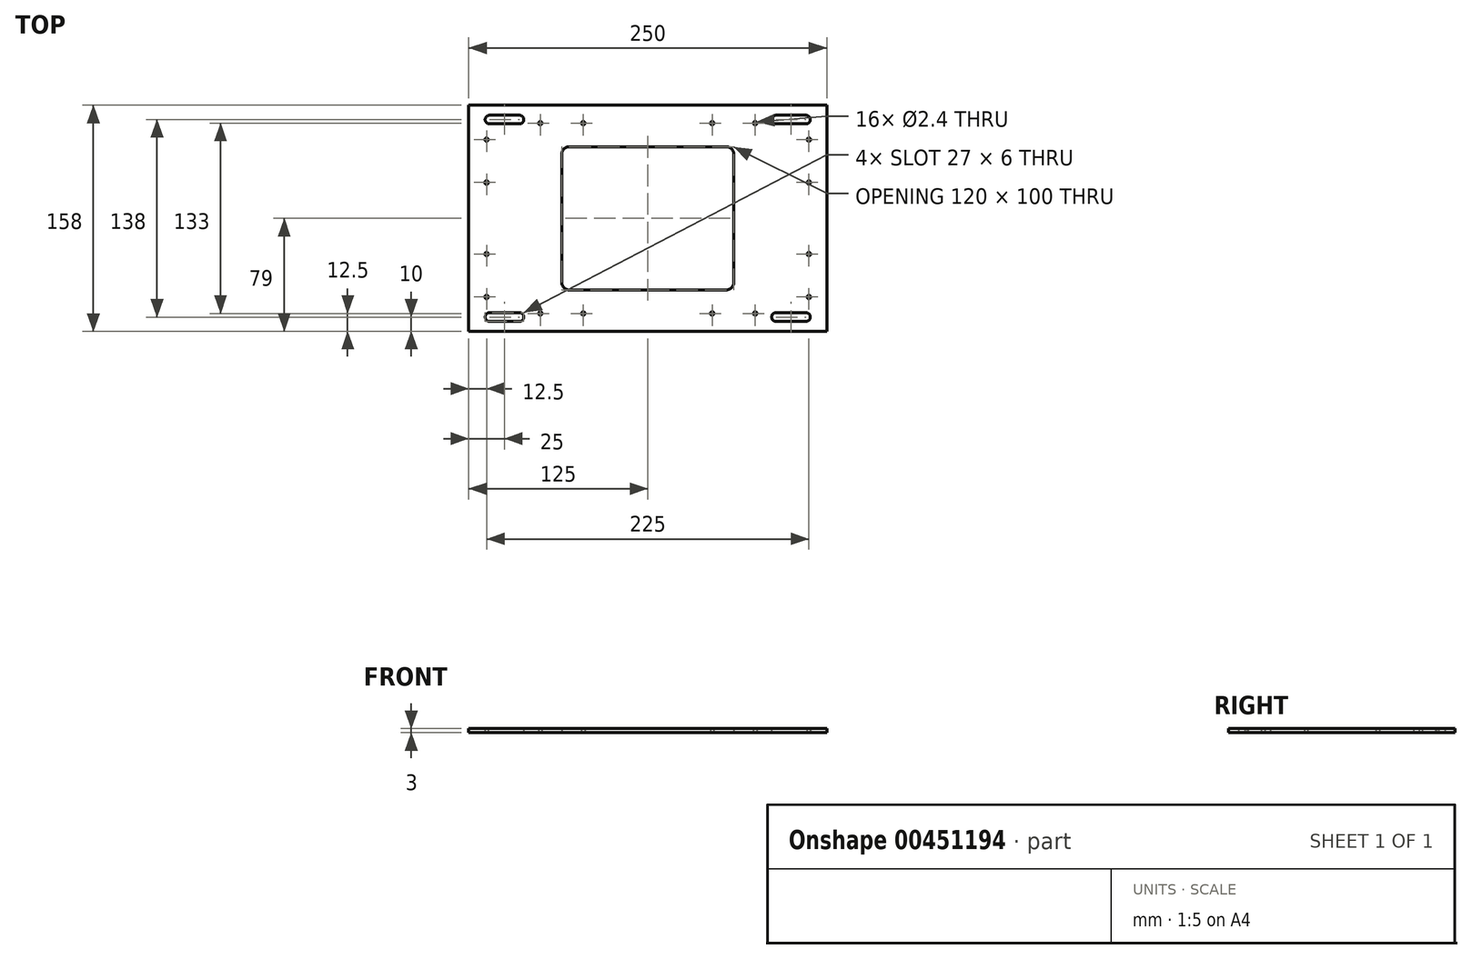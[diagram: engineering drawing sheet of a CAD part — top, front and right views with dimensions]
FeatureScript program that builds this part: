
annotation { "Feature Type Name" : "Feature", "Feature Type Description" : "" }
export const myFeature = defineFeature(function(context is Context, id is Id, definition is map)
    precondition{}
    {
        {
            var Q0;
            Q0=qCreatedBy(makeId("Top.planeOp"),FACE);
            var sketch = newSketch(context, id + "F0", { "sketchPlane" : qUnion([Q0])});
            skLineSegment(sketch, "E0.bottom", {"start": v(125, -79) * mm, "end": v(-125, -79) * mm});
            skLineSegment(sketch, "E0.top", {"start": v(125, 79) * mm, "end": v(-125, 79) * mm});
            skLineSegment(sketch, "E0.left", {"start": v(125, -79) * mm, "end": v(125, 79) * mm});
            skLineSegment(sketch, "E0.right", {"start": v(-125, -79) * mm, "end": v(-125, 79) * mm});
            skPoint(sketch, "E0.middle", {"position": v(0, 0) * mm});
            skCircle(sketch, "E1", {"center": v(-107.5, 69) * mm, "radius": 2.5 * mm, "construction": true});
            skCircle(sketch, "E2", {"center": v(-107.5, -69) * mm, "radius": 2.5 * mm, "construction": true});
            skLineSegment(sketch, "E3.bottom", {"start": v(60, -50) * mm, "end": v(-60, -50) * mm});
            skLineSegment(sketch, "E3.top", {"start": v(60, 50) * mm, "end": v(-60, 50) * mm});
            skLineSegment(sketch, "E3.left", {"start": v(60, -50) * mm, "end": v(60, 50) * mm});
            skLineSegment(sketch, "E3.right", {"start": v(-60, -50) * mm, "end": v(-60, 50) * mm});
            skCircle(sketch, "E4.MirrorC", {"center": v(107.5, -69) * mm, "radius": 2.5 * mm, "construction": true});
            skCircle(sketch, "E5.MirrorC", {"center": v(107.5, 69) * mm, "radius": 2.5 * mm, "construction": true});
            skCircle(sketch, "E6", {"center": v(-112.5, 55) * mm, "radius": 1.2 * mm});
            skCircle(sketch, "E7", {"center": v(-112.5, 25) * mm, "radius": 1.2 * mm});
            skCircle(sketch, "E8", {"center": v(-112.5, -25) * mm, "radius": 1.2 * mm});
            skCircle(sketch, "E9", {"center": v(-112.5, -55) * mm, "radius": 1.2 * mm});
            skCircle(sketch, "E10.MirrorC", {"center": v(112.5, -25) * mm, "radius": 1.2 * mm});
            skCircle(sketch, "E11.MirrorC", {"center": v(112.5, -55) * mm, "radius": 1.2 * mm});
            skCircle(sketch, "E12.MirrorC", {"center": v(112.5, 25) * mm, "radius": 1.2 * mm});
            skCircle(sketch, "E13.MirrorC", {"center": v(112.5, 55) * mm, "radius": 1.2 * mm});
            skCircle(sketch, "E14", {"center": v(-75, -66.5) * mm, "radius": 1.2 * mm});
            skCircle(sketch, "E15", {"center": v(-45, -66.5) * mm, "radius": 1.2 * mm});
            skCircle(sketch, "E16", {"center": v(45, -66.5) * mm, "radius": 1.2 * mm});
            skCircle(sketch, "E17", {"center": v(75, -66.5) * mm, "radius": 1.2 * mm});
            skCircle(sketch, "E18.MirrorC", {"center": v(45, 66.5) * mm, "radius": 1.2 * mm});
            skCircle(sketch, "E19.MirrorC", {"center": v(-75, 66.5) * mm, "radius": 1.2 * mm});
            skCircle(sketch, "E20.MirrorC", {"center": v(-45, 66.5) * mm, "radius": 1.2 * mm});
            skCircle(sketch, "E21.MirrorC", {"center": v(75, 66.5) * mm, "radius": 1.2 * mm});
            skLineSegment(sketch, "E22.bottom", {"start": v(-89.5, 66) * mm, "end": v(-110.5, 66) * mm});
            skLineSegment(sketch, "E22.top", {"start": v(-89.5, 72) * mm, "end": v(-110.5, 72) * mm});
            skLineSegment(sketch, "E22.left", {"start": v(-89.5, 66) * mm, "end": v(-89.5, 72) * mm, "construction": true});
            skLineSegment(sketch, "E22.right", {"start": v(-110.5, 66) * mm, "end": v(-110.5, 72) * mm, "construction": true});
            skPoint(sketch, "E22.middle", {"position": v(-100, 69) * mm});
            skArc(sketch, "E23", {"start": v(-89.5, 66) * mm, "mid": v(-86.5, 69) * mm, "end": v(-89.5, 72) * mm});
            skArc(sketch, "E24", {"start": v(-110.5, 72) * mm, "mid": v(-113.5, 69) * mm, "end": v(-110.5, 66) * mm});
            skCircle(sketch, "E25", {"center": v(-91.5, 69) * mm, "radius": 2.5 * mm, "construction": true});
            skLineSegment(sketch, "E26.bottom", {"start": v(110.5, 66) * mm, "end": v(89.5, 66) * mm});
            skLineSegment(sketch, "E26.top", {"start": v(110.5, 72) * mm, "end": v(89.5, 72) * mm});
            skLineSegment(sketch, "E26.left", {"start": v(110.5, 66) * mm, "end": v(110.5, 72) * mm});
            skLineSegment(sketch, "E26.right", {"start": v(89.5, 66) * mm, "end": v(89.5, 72) * mm});
            skPoint(sketch, "E26.middle", {"position": v(100, 69) * mm});
            skArc(sketch, "E27", {"start": v(89.5, 72) * mm, "mid": v(86.5, 69) * mm, "end": v(89.5, 66) * mm});
            skArc(sketch, "E28", {"start": v(110.5, 66) * mm, "mid": v(113.5, 69) * mm, "end": v(110.5, 72) * mm});
            skLineSegment(sketch, "E29.MirrorCS", {"start": v(89.5, -66) * mm, "end": v(89.5, -72) * mm});
            skLineSegment(sketch, "E30.MirrorCS", {"start": v(110.5, -66) * mm, "end": v(110.5, -72) * mm});
            skArc(sketch, "E31.MirrorCS", {"start": v(89.5, -72) * mm, "mid": v(86.5, -69) * mm, "end": v(89.5, -66) * mm});
            skLineSegment(sketch, "E32.MirrorCS", {"start": v(110.5, -72) * mm, "end": v(89.5, -72) * mm});
            skLineSegment(sketch, "E33.MirrorCS", {"start": v(110.5, -66) * mm, "end": v(89.5, -66) * mm});
            skArc(sketch, "E34.MirrorCS", {"start": v(110.5, -66) * mm, "mid": v(113.5, -69) * mm, "end": v(110.5, -72) * mm});
            skPoint(sketch, "E35.MirrorP", {"position": v(100, -69) * mm});
            skLineSegment(sketch, "E36.MirrorCS", {"start": v(-89.5, -72) * mm, "end": v(-110.5, -72) * mm});
            skLineSegment(sketch, "E37.MirrorCS", {"start": v(-110.5, -66) * mm, "end": v(-110.5, -72) * mm, "construction": true});
            skLineSegment(sketch, "E38.MirrorCS", {"start": v(-89.5, -66) * mm, "end": v(-89.5, -72) * mm, "construction": true});
            skArc(sketch, "E39.MirrorCS", {"start": v(-110.5, -72) * mm, "mid": v(-113.5, -69) * mm, "end": v(-110.5, -66) * mm});
            skArc(sketch, "E40.MirrorCS", {"start": v(-89.5, -66) * mm, "mid": v(-86.5, -69) * mm, "end": v(-89.5, -72) * mm});
            skLineSegment(sketch, "E41.MirrorCS", {"start": v(-89.5, -66) * mm, "end": v(-110.5, -66) * mm});
            skPoint(sketch, "E42.MirrorP", {"position": v(-100, -69) * mm});
            skSolve(sketch);
        }
        {
            var Q0;
            Q0 = qSketchRegion(id + "F0", true);
            extrude(context, id + "F1", {"entities" : qUnion([Q0]), "depth" : 3 * mm, "offsetDistance" : 25 * mm});
        }
        {
            var Q0;
            Q0=makeQuery(id+"F1.opExtrude","SWEPT_EDGE",EDGE,{"disambiguationData":[OSD([sQuery(id+"F0.wireOp",EDGE,"E3.top"),sQuery(id+"F0.wireOp",EDGE,"E3.right")])]});
            var Q1;
            Q1=makeQuery(id+"F1.opExtrude","SWEPT_EDGE",EDGE,{"disambiguationData":[OSD([sQuery(id+"F0.wireOp",EDGE,"E3.bottom"),sQuery(id+"F0.wireOp",EDGE,"E3.right")])]});
            var Q2;
            Q2=makeQuery(id+"F1.opExtrude","SWEPT_EDGE",EDGE,{"disambiguationData":[OSD([sQuery(id+"F0.wireOp",EDGE,"E3.bottom"),sQuery(id+"F0.wireOp",EDGE,"E3.left")])]});
            var Q3;
            Q3=makeQuery(id+"F1.opExtrude","SWEPT_EDGE",EDGE,{"disambiguationData":[OSD([sQuery(id+"F0.wireOp",EDGE,"E3.top"),sQuery(id+"F0.wireOp",EDGE,"E3.left")])]});
            fillet(context, id + "F2", {"entities" : qUnion([Q0, Q1, Q2, Q3]), "tangentPropagation" : true, "radius" : 5 * mm, "defaultsChanged" : false, "vertexSettings" : [], "allowEdgeOverflow" : false});
        }
    });
